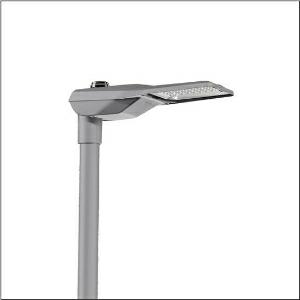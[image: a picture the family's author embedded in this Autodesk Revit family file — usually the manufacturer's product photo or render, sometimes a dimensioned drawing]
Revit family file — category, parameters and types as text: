
# Revit family: streetlight_sl_21_mini___pl52_5xe6h47n08hb_96c1
name_source: partatom
category: Lighting Fixtures
units: mm (PartAtom-declared; Revit-internal decimal feet)

## family parameters
Cut with Voids When Loaded = No
Host = Face
Light Source = No
Part Type = Normal
Room Calculation Point = No
Round Connector Dimension = Use Diameter
Shared = No

## types (1)
- --- (1 x LED, 9260 lm, 66 W, 4000K)
    Apparent Load = 66 VA
    CIE Flux Codes = 27 59 98 100 100
    Color Rendering = 70
    Color Temperature = 4000K
    Default Elevation = 1800 mm
    Description = Streetlight SL 21 mini, mast luminaire, primary light control with lens, of PMMA, primary optical cover: cover, of toughened safety glass, transparent, light distribution: PL52, light emission: direct distribution, primary light characteristic: asymmetric, installation type: side-entry, LED, 3G 1.5mm², High Power LED, rated luminous flux: 9.260lm, luminous efficacy: 140lm/W, light colour: 740, colour temperature: 4000K, control gear: NEMA (7pin), control: overheat protection, pre-setting: linear dimming characteristic, constant luminous flux control, time-dependent luminous flux control, flexible luminous flux parameterisation, mains connection: 230..240V, AC, 50/60Hz, connection cable pre-assembled, cable length: 8,5m, wiring characteristics: H07RN-F, start of lifetime: 66W, end of service life: 69W, reduction: 30W, luminaire housing, of diecast aluminium (EN AC-44300), powder-coated, Siteco® metallic grey (DB 702S), corrosivity category C5 mid according to DIN EN ISO 12944, multi-level sealing system, sealing non-destructively replaceable, inclination adjustable: 0°, 5°, 10°, 15°, length: 628mm, width: 235mm, height: 110mm, spigot size: 42mm (side-entry), mounting height: 4..8m, protection rating (complete): IP66, insulation class (complete): insulation class I (protective earthing), certification: CE, ENEC, ENEC+, VDE, impact resistance: IK10, permissible operating ambient temperature for outdoor applications: -40..+50°C, standard-compliant lighting for roads and squares, packaging unit: 1 piece

Light Distribution: PL52
    Height = 110 mm
    Lamp = 1 x LED
    Lamp Light Flux = 9260 lm
    Lamp Power = 66 W
    Lamp count = 1
    Length = 625 mm
    Luminous efficacy = 140 lm/W
    Manufacturer = Siteco
    ModVariant = No
    Model = 5XE6H47N08HB
    Number of Poles = 1
    OnlyDefault = Yes
    Power Factor = 1
    Product Name = Streetlight SL 21 mini | PL52
    Product group = mast luminaire | pylon top
    ProductGroupID = 6100
    Protection Class = Protection class I
    Protection Degree = IP 66
    RLX_Detail_Level = 1
    RLX_Emergency_Light_Flux = 0 lm
    RLX_Emergency_Type = 0
    RLX_Emergency_Type_DB = No
    RlxData = <blob elided: 35717 chars, md5=f49b119f>
    Socket = socket
    Standby Power = 0 W
    System Light Flux = 9260 lm
    System Power = 66 W
    Type Comments = factory setting: luminous flux: 100 % | dim-lin: 254 | 670 mA
    Type Image = l_1294379.jpg
    URL = http://relux.com
    VarID = @adj_136966
    Voltage = 0 V
    Weight = 0.00 kg
    Width = 234 mm

## geometry (parser evidence)
native form markers: Blend x4, Sweep x10
no freeform markers — native parametric forms only
